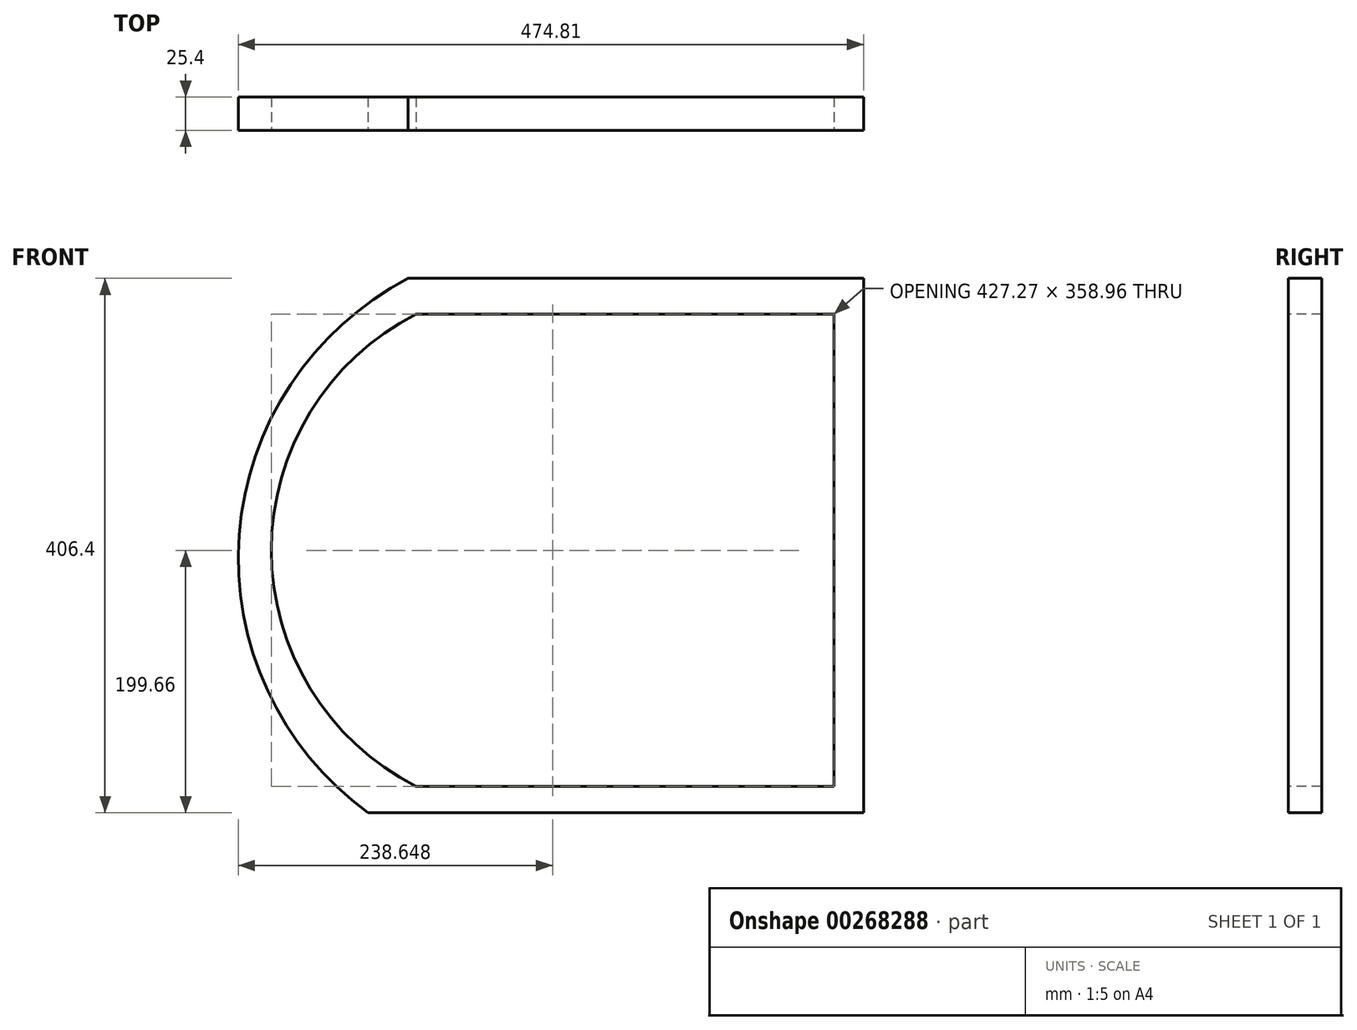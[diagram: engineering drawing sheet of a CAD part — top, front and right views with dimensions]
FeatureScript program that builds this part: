
annotation { "Feature Type Name" : "Feature", "Feature Type Description" : "" }
export const myFeature = defineFeature(function(context is Context, id is Id, definition is map)
    precondition{}
    {
        {
            var Q0;
            Q0=qCreatedBy(makeId("Front.planeOp"),FACE);
            var sketch = newSketch(context, id + "F0", { "sketchPlane" : qUnion([Q0])});
            skLineSegment(sketch, "E0.bottom", {"start": v(235.02, 212.64) * mm, "end": v(-239.8, 212.64) * mm});
            skLineSegment(sketch, "E0.top", {"start": v(235.02, -193.76) * mm, "end": v(-239.8, -193.76) * mm});
            skLineSegment(sketch, "E0.left", {"start": v(235.02, 212.64) * mm, "end": v(235.02, -193.76) * mm});
            skLineSegment(sketch, "E0.right", {"start": v(-239.8, 212.64) * mm, "end": v(-239.8, -193.76) * mm});
            skSolve(sketch);
        }
        {
            var Q0;
            Q0 = qSketchRegion(id + "F0", true);
            var Q1;
            Q1=makeQuery(id+"F0.imprint","IMPRINT",FACE,{"disambiguationData":[TD([[makeQuery(id+"F0.imprint","IMPRINT",EDGE,{"derivedFrom":sQuery(id+"F0.wireOp",EDGE,"E0.bottom")}),1.0]])]});
            extrude(context, id + "F1", {"entities" : qUnion([Q0, Q1]), "depth" : 25.4 * mm});
        }
        {
            var Q0;
            Q0=makeQuery(id+"F1.opExtrude","CAP_FACE",FACE,{"disambiguationData":[OSD([sQuery(id+"F0.wireOp",EDGE,"E0.bottom"),sQuery(id+"F0.wireOp",EDGE,"E0.top"),sQuery(id+"F0.wireOp",EDGE,"E0.left"),sQuery(id+"F0.wireOp",EDGE,"E0.right")])],"isStart":false});
            var sketch = newSketch(context, id + "F2", { "sketchPlane" : qUnion([Q0])});
            skCircle(sketch, "E1", {"center": v(0, 0) * mm, "radius": 239.8 * mm});
            skSolve(sketch);
        }
        {
            var Q0;
            {var subQ0=sQuery(id+"F2.wireOp",EDGE,"E1");var subQ1=makeQuery(id+"F1.opExtrude","CAP_EDGE",EDGE,{"disambiguationData":[OSD([sQuery(id+"F0.wireOp",EDGE,"E0.bottom")])],"isStart":false});var subQ2=makeQuery(id+"F2.imprint","INTERSECT",VERTEX,{"disambiguationData":[OD(1.0)],"derivedFrom":[subQ1,subQ0]});Q0=makeQuery(id+"F2.imprint","IMPRINT",FACE,{"disambiguationData":[TD([[makeQuery(id+"F2.imprint","IMPRINT",EDGE,{"disambiguationData":[TD([[subQ2,-1.0]])],"derivedFrom":subQ0}),-1.0]])]});}
            var Q1;
            {var subQ0=sQuery(id+"F2.wireOp",EDGE,"E1");var subQ1=makeQuery(id+"F1.opExtrude","CAP_EDGE",EDGE,{"disambiguationData":[OSD([sQuery(id+"F0.wireOp",EDGE,"E0.right")])],"isStart":false});var subQ2=makeQuery(id+"F2.imprint","INTERSECT",VERTEX,{"derivedFrom":[subQ1,subQ0]});Q1=makeQuery(id+"F2.imprint","IMPRINT",FACE,{"disambiguationData":[TD([[makeQuery(id+"F2.imprint","IMPRINT",EDGE,{"disambiguationData":[TD([[subQ2,-1.0]])],"derivedFrom":subQ0}),-1.0]])]});}
            extrude(context, id + "F3", {"entities" : qUnion([Q0, Q1]), "operationType" : NewBodyOperationType.REMOVE, "oppositeDirection" : true, "depth" : 25.4 * mm});
        }
        {
            var Q0;
            Q0=makeQuery(id+"F1.opExtrude","CAP_FACE",FACE,{"disambiguationData":[OSD([sQuery(id+"F0.wireOp",EDGE,"E0.bottom"),sQuery(id+"F0.wireOp",EDGE,"E0.top"),sQuery(id+"F0.wireOp",EDGE,"E0.left"),sQuery(id+"F0.wireOp",EDGE,"E0.right")])],"isStart":false});
            var sketch = newSketch(context, id + "F4", { "sketchPlane" : qUnion([Q0])});
            skLineSegment(sketch, "E2.bottom", {"start": v(212.5, 185.38) * mm, "end": v(-105.01, 185.38) * mm});
            skLineSegment(sketch, "E2.top", {"start": v(212.5, -173.58) * mm, "end": v(-105.01, -173.58) * mm});
            skLineSegment(sketch, "E2.left", {"start": v(212.5, 185.38) * mm, "end": v(212.5, -173.58) * mm});
            skLineSegment(sketch, "E2.right", {"start": v(-105.01, 185.38) * mm, "end": v(-105.01, -173.58) * mm});
            skSolve(sketch);
        }
        {
            var Q0;
            Q0 = qSketchRegion(id + "F4", true);
            extrude(context, id + "F5", {"entities" : qUnion([Q0]), "operationType" : NewBodyOperationType.REMOVE, "oppositeDirection" : true, "depth" : 25.4 * mm});
        }
        {
            var Q0;
            Q0=makeQuery(id+"F1.opExtrude","CAP_FACE",FACE,{"disambiguationData":[OSD([sQuery(id+"F0.wireOp",EDGE,"E0.bottom"),sQuery(id+"F0.wireOp",EDGE,"E0.top"),sQuery(id+"F0.wireOp",EDGE,"E0.left"),sQuery(id+"F0.wireOp",EDGE,"E0.right")])],"isStart":false});
            var sketch = newSketch(context, id + "F6", { "sketchPlane" : qUnion([Q0])});
            skArc(sketch, "E3", {"start": v(-105.01, 185.38) * mm, "mid": v(-214.78, 5.9) * mm, "end": v(-105.01, -173.58) * mm});
            skSolve(sketch);
        }
        {
            var Q0;
            Q0=makeQuery(id+"F6.imprint","IMPRINT",FACE,{"disambiguationData":[TD([[makeQuery(id+"F6.imprint","IMPRINT",EDGE,{"derivedFrom":sQuery(id+"F6.wireOp",EDGE,"E3")}),1.0]])]});
            extrude(context, id + "F7", {"entities" : qUnion([Q0]), "operationType" : NewBodyOperationType.REMOVE, "oppositeDirection" : true, "depth" : 25.4 * mm});
        }
    });
